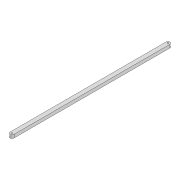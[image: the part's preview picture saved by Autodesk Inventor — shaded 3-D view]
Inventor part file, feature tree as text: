
AUTODESK INVENTOR PART (.ipt)
format: ipt  version: 2022 (Build 260153000, 153)  size: 88,576 bytes
history: native  units: mm
features: extrude x1, sketch x1
ambient origin geometry x8: Origin, YZ Plane, XZ Plane, XY Plane, X Axis, Y Axis, Z Axis, Center Point
bodies: Solid1 (feature_tree)
feature tree (2):
  extrude  "Extrusion1"  Depth=10.0mm
  sketch  "Sketch1"  dims[d0=388.032mm d1=10.0mm d2=3.0mm d3=3.0mm d4=8.0mm d5=0.0mm]
